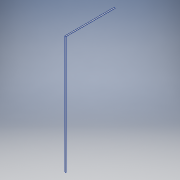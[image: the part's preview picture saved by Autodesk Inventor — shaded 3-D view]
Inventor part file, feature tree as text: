
AUTODESK INVENTOR PART (.ipt)
format: ipt  version: 2019 (Build 230136000, 136)  size: 108,032 bytes
history: native  units: in
note: dims shown in document units (in); Inventor stores cm internally (conversion verified against a paired STEP export)
features: extrude x2, sketch x2
ambient origin geometry x8: Origin, YZ Plane, XZ Plane, XY Plane, X Axis, Y Axis, Z Axis, Center Point
bodies: Solid1 (feature_tree)
feature tree (4):
  extrude  "Extrusion1"  Depth=0.5in
  extrude  "Extrusion2"  Depth=0.5in
  sketch  "Sketch1"  dims[d0=19.685in d2=0.5in]
  sketch  "Sketch2"  dims[d3=0.063in d4=0.0in d7=0.5in d8=0.063in d9=0.5in d10=0.063in d11=47.2441in d12=0.0in]
